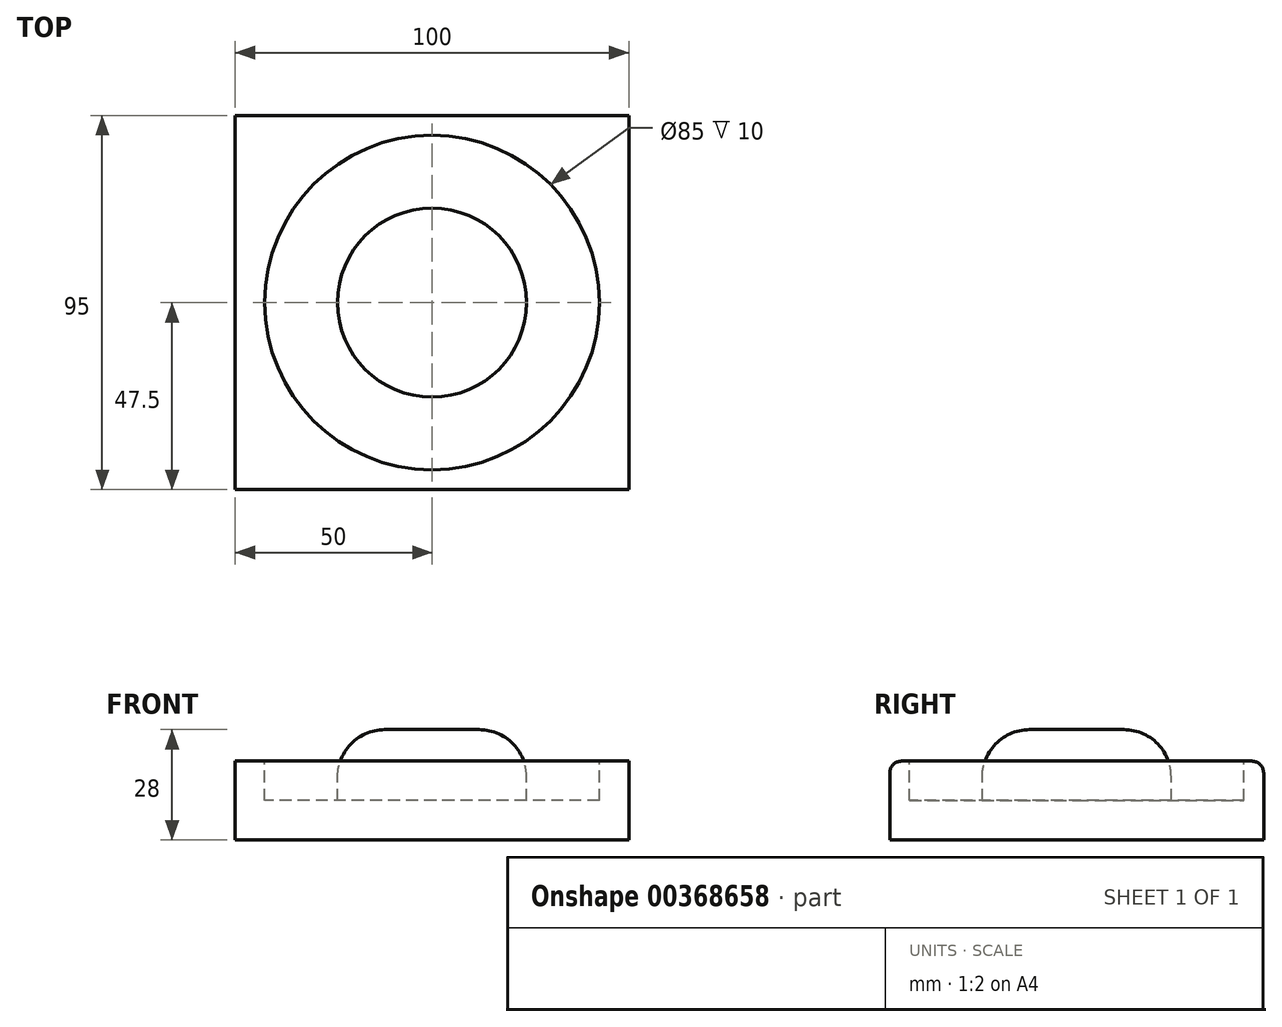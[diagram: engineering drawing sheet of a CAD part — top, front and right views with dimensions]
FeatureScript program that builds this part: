
annotation { "Feature Type Name" : "Feature", "Feature Type Description" : "" }
export const myFeature = defineFeature(function(context is Context, id is Id, definition is map)
    precondition{}
    {
        {
            var Q0;
            Q0=qCreatedBy(makeId("Top.planeOp"),FACE);
            var sketch = newSketch(context, id + "F0", { "sketchPlane" : qUnion([Q0])});
            skLineSegment(sketch, "E0.bottom", {"start": v(-50, 47.5) * mm, "end": v(50, 47.5) * mm});
            skLineSegment(sketch, "E0.top", {"start": v(-50, -47.5) * mm, "end": v(50, -47.5) * mm});
            skLineSegment(sketch, "E0.left", {"start": v(-50, 47.5) * mm, "end": v(-50, -47.5) * mm});
            skLineSegment(sketch, "E0.right", {"start": v(50, 47.5) * mm, "end": v(50, -47.5) * mm});
            skPoint(sketch, "E0.middle", {"position": v(0, 0) * mm});
            skSolve(sketch);
        }
        {
            var Q0;
            Q0=makeQuery(id+"F0.imprint","IMPRINT",FACE,{"disambiguationData":[TD([[makeQuery(id+"F0.imprint","IMPRINT",EDGE,{"derivedFrom":sQuery(id+"F0.wireOp",EDGE,"E0.bottom")}),-1.0]])]});
            extrude(context, id + "F1", {"entities" : qUnion([Q0]), "endBound" : BoundingType.SYMMETRIC, "depth" : 20 * mm});
        }
        {
            var Q0;
            Q0=makeQuery(id+"F1.opExtrude","CAP_FACE",FACE,{"disambiguationData":[OSD([sQuery(id+"F0.wireOp",EDGE,"E0.bottom"),sQuery(id+"F0.wireOp",EDGE,"E0.top"),sQuery(id+"F0.wireOp",EDGE,"E0.left"),sQuery(id+"F0.wireOp",EDGE,"E0.right")])],"isStart":false});
            var sketch = newSketch(context, id + "F2", { "sketchPlane" : qUnion([Q0])});
            skCircle(sketch, "E1", {"center": v(0, 0) * mm, "radius": 42.5 * mm});
            skCircle(sketch, "E2", {"center": v(0, 0) * mm, "radius": 24 * mm});
            skCircle(sketch, "E3", {"center": v(0, 0) * mm, "radius": 14 * mm});
            skSolve(sketch);
        }
        {
            var Q0;
            Q0=makeQuery(id+"F2.imprint","IMPRINT",FACE,{"disambiguationData":[TD([[makeQuery(id+"F2.imprint","IMPRINT",EDGE,{"derivedFrom":sQuery(id+"F2.wireOp",EDGE,"E1")}),1.0]])]});
            extrude(context, id + "F3", {"entities" : qUnion([Q0]), "operationType" : NewBodyOperationType.REMOVE, "oppositeDirection" : true, "depth" : 10 * mm});
        }
        {
            var Q0;
            Q0=makeQuery(id+"F3.boolean.opBoolean","SPLIT",FACE,{"disambiguationData":[TD([makeQuery(id+"F3.opExtrude","SWEPT_FACE",FACE,{"disambiguationData":[OSD([sQuery(id+"F2.wireOp",EDGE,"E2")])]})])],"derivedFrom":makeQuery(id+"F1.opExtrude","CAP_FACE",FACE,{"disambiguationData":[OSD([sQuery(id+"F0.wireOp",EDGE,"E0.bottom"),sQuery(id+"F0.wireOp",EDGE,"E0.top"),sQuery(id+"F0.wireOp",EDGE,"E0.left"),sQuery(id+"F0.wireOp",EDGE,"E0.right")])],"isStart":false})});
            var sketch = newSketch(context, id + "F4", { "sketchPlane" : qUnion([Q0])});
            skCircle(sketch, "E4", {"center": v(0, 0) * mm, "radius": 14 * mm});
            skSolve(sketch);
        }
        {
            var Q0;
            Q0=makeQuery(id+"F4.imprint","IMPRINT",FACE,{"disambiguationData":[TD([[makeQuery(id+"F4.imprint","IMPRINT",EDGE,{"derivedFrom":sQuery(id+"F4.wireOp",EDGE,"E4")}),-1.0]])]});
            var Q1;
            Q1=makeQuery(id+"F4.imprint","IMPRINT",FACE,{"disambiguationData":[TD([[makeQuery(id+"F4.imprint","IMPRINT",EDGE,{"derivedFrom":sQuery(id+"F4.wireOp",EDGE,"E4")}),1.0]])]});
            extrude(context, id + "F5", {"entities" : qUnion([Q0, Q1]), "operationType" : NewBodyOperationType.ADD, "depth" : 8 * mm});
        }
        {
            var Q0;
            Q0=makeQuery(id+"F5.opExtrude","CAP_EDGE",EDGE,{"disambiguationData":[OSD([sQuery(id+"F2.wireOp",EDGE,"E2")])],"isStart":false});
            fillet(context, id + "F6", {"entities" : qUnion([Q0]), "radius" : 12 * mm, "tangentPropagation" : true, "allowEdgeOverflow" : false});
        }
        {
            var Q0;
            Q0=makeQuery(id+"F1.opExtrude","CAP_EDGE",EDGE,{"disambiguationData":[OSD([sQuery(id+"F0.wireOp",EDGE,"E0.bottom")])],"isStart":false});
            var Q1;
            Q1=makeQuery(id+"F1.opExtrude","CAP_EDGE",EDGE,{"disambiguationData":[OSD([sQuery(id+"F0.wireOp",EDGE,"E0.top")])],"isStart":false});
            fillet(context, id + "F7", {"entities" : qUnion([Q0, Q1]), "radius" : 3 * mm, "tangentPropagation" : true, "allowEdgeOverflow" : false});
        }
    });
